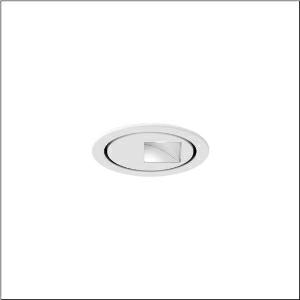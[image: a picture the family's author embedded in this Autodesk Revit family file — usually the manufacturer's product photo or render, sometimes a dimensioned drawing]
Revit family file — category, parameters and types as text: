
# Revit family: lunis_11_micro_round_51dj11cd1wm21
name_source: partatom
category: Lighting Fixtures
units: mm (PartAtom-declared; Revit-internal decimal feet)

## family parameters
Cut with Voids When Loaded = No
Host = Face
Light Source = No
Part Type = Normal
Room Calculation Point = No
Round Connector Dimension = Use Diameter
Shared = No

## types (1)
- Lunis 11 micro round (1 x LED 3000K / CRI = 90 (unbekannt), 1100 lm, 3000K)
    Apparent Load = 20 VA
    CIE Flux Codes = 42 75 96 100 100
    Color Rendering = 90
    Color Temperature = 3000K
    Default Elevation = 1800 mm
    Description = Lunis 11 micro round, downlight, light control with wallwasher, of highly reflective aluminium, highly specular, light emission: direct distribution, LED rated luminous flux: 1.100lm, light colour: 930, with terminal, 5-pole, mains connection: 220..230V, AC, 50/60Hz, LED module, of aluminium, highly specular, white, diameter: 114mm, clamping range: 1..40mm, recessing ring, of plastic, traffic white (RAL 9016), protection rating (complete): IP20, insulation class (complete): insulation class II (safety insulation), certification: CE, permissible ambient temperature for indoor applications: 0..+35°C, packaging unit: 1 piece
    Height = 0 mm  [stored 0 ft]
    Lamp = 1 x LED 3000K / CRI >= 90 (unbekannt)
    Lamp Light Flux = 1100 lm
    Lamp count = 1
    Length = 114 mm
    Luminous efficacy = 56 lm/W
    Manufacturer = Siteco
    ModVariant = No
    Model = 51DJ11CD1WM21
    Mounting Place = Ceiling
    Mounting Type = Recessed
    Number of Poles = 1
    OnlyDefault = Yes
    Power Factor = 1
    Product Name = Lunis 11 micro round
    Product group = downlight
    ProductGroupID = 400
    Protection Class = Protection class II
    Protection Degree = IP 20
    RLX_Detail_Level = 1
    RLX_Emergency_Light_Flux = 0 lm
    RLX_Emergency_Type = 0
    RLX_Emergency_Type_DB = No
    RlxData = <blob elided: 40057 chars, md5=58290c95>
    Socket = socket
    Standby Power = 0 W
    System Light Flux = 1100 lm
    System Power = 20 W
    Type Comments = Product without accessories
    Type Image = l_1004773.jpg
    URL = http://relux.com
    VarID = ---
    Voltage = 0 V
    Weight = 0.00 kg
    Width = 114 mm

note: [stored X ft] marks values corroborated as IEEE doubles in the binary element streams (Revit-internal decimal feet)

## geometry (parser evidence)
native form markers: Blend x4, Sweep x10
no freeform markers — native parametric forms only
